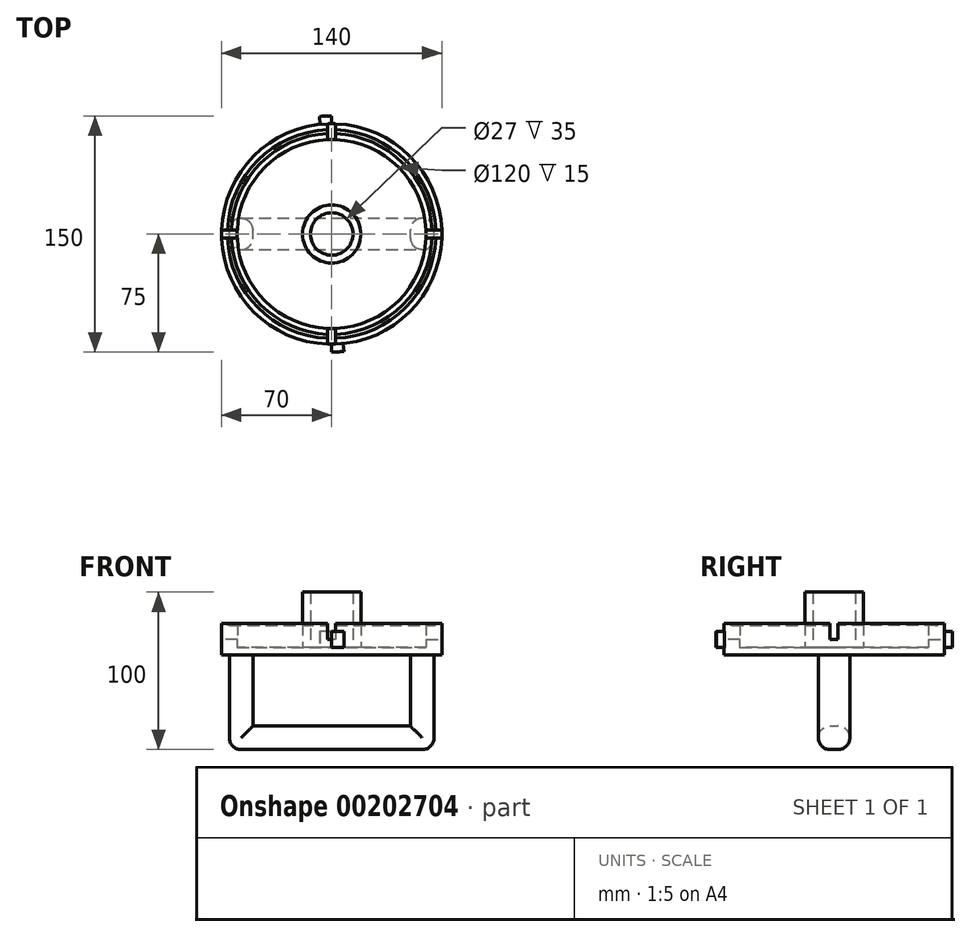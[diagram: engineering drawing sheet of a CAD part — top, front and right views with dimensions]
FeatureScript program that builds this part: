
annotation { "Feature Type Name" : "Feature", "Feature Type Description" : "" }
export const myFeature = defineFeature(function(context is Context, id is Id, definition is map)
    precondition{}
    {
        {
            var Q0;
            Q0=qCreatedBy(makeId("Top.planeOp"),FACE);
            var sketch = newSketch(context, id + "F0", { "sketchPlane" : qUnion([Q0])});
            skCircle(sketch, "E0", {"center": v(0, 0) * mm, "radius": 13.5 * mm});
            skCircle(sketch, "E1", {"center": v(0, 0) * mm, "radius": 18.5 * mm});
            skCircle(sketch, "E2", {"center": v(0, 0) * mm, "radius": 60 * mm});
            skCircle(sketch, "E3", {"center": v(0, 0) * mm, "radius": 70 * mm});
            skCircle(sketch, "E4", {"center": v(0, 0) * mm, "radius": 75 * mm});
            skLineSegment(sketch, "E5", {"start": v(0, 0) * mm, "end": v(0, 75) * mm});
            skLineSegment(sketch, "E6", {"start": v(0, 0) * mm, "end": v(0, -75) * mm});
            skLineSegment(sketch, "E7", {"start": v(0, 0) * mm, "end": v(-7.84, 74.59) * mm});
            skLineSegment(sketch, "E8", {"start": v(0, 0) * mm, "end": v(7.84, -74.59) * mm});
            skLineSegment(sketch, "E9.bottom", {"start": v(2.5, 2.5) * mm, "end": v(-2.5, 2.5) * mm});
            skLineSegment(sketch, "E9.top", {"start": v(2.5, -2.5) * mm, "end": v(-2.5, -2.5) * mm});
            skLineSegment(sketch, "E9.left", {"start": v(2.5, 2.5) * mm, "end": v(2.5, -2.5) * mm});
            skLineSegment(sketch, "E9.right", {"start": v(-2.5, 2.5) * mm, "end": v(-2.5, -2.5) * mm});
            skLineSegment(sketch, "E10", {"start": v(-2.5, -2.5) * mm, "end": v(-69.96, -2.5) * mm});
            skLineSegment(sketch, "E11", {"start": v(-2.5, 2.5) * mm, "end": v(-69.96, 2.5) * mm});
            skLineSegment(sketch, "E12", {"start": v(2.5, -2.5) * mm, "end": v(69.96, -2.5) * mm});
            skLineSegment(sketch, "E13", {"start": v(2.5, 2.5) * mm, "end": v(69.96, 2.5) * mm});
            skLineSegment(sketch, "E14", {"start": v(-2.5, -2.5) * mm, "end": v(-2.5, -69.96) * mm});
            skPoint(sketch, "E15.endSnap0", {"position": v(3.92, -37.3) * mm});
            skLineSegment(sketch, "E16", {"start": v(-2.5, 2.5) * mm, "end": v(-2.5, 69.96) * mm});
            skLineSegment(sketch, "E17", {"start": v(2.5, 2.5) * mm, "end": v(2.5, 69.96) * mm});
            skLineSegment(sketch, "E18", {"start": v(2.5, -2.5) * mm, "end": v(2.5, -69.96) * mm});
            skSolve(sketch);
        }
        {
            var Q0;
            {var subQ0=sQuery(id+"F0.wireOp",EDGE,"E5");var subQ1=sQuery(id+"F0.wireOp",EDGE,"E0");var subQ2=makeQuery(id+"F0.imprint","INTERSECT",VERTEX,{"derivedFrom":[subQ1,subQ0]});Q0=makeQuery(id+"F0.imprint","IMPRINT",FACE,{"disambiguationData":[TD([[makeQuery(id+"F0.imprint","IMPRINT",EDGE,{"disambiguationData":[TD([[subQ2,-1.0]])],"derivedFrom":subQ1}),1.0]])]});}
            var Q1;
            {var subQ0=sQuery(id+"F0.wireOp",EDGE,"E7");var subQ1=sQuery(id+"F0.wireOp",EDGE,"E0");var subQ2=makeQuery(id+"F0.imprint","INTERSECT",VERTEX,{"derivedFrom":[subQ1,subQ0]});Q1=makeQuery(id+"F0.imprint","IMPRINT",FACE,{"disambiguationData":[TD([[makeQuery(id+"F0.imprint","IMPRINT",EDGE,{"disambiguationData":[TD([[subQ2,-1.0]])],"derivedFrom":subQ1}),1.0]])]});}
            var Q2;
            {var subQ0=sQuery(id+"F0.wireOp",EDGE,"E17");var subQ1=sQuery(id+"F0.wireOp",EDGE,"E0");var subQ2=makeQuery(id+"F0.imprint","INTERSECT",VERTEX,{"derivedFrom":[subQ1,subQ0]});Q2=makeQuery(id+"F0.imprint","IMPRINT",FACE,{"disambiguationData":[TD([[makeQuery(id+"F0.imprint","IMPRINT",EDGE,{"disambiguationData":[TD([[subQ2,-1.0]])],"derivedFrom":subQ1}),1.0]])]});}
            var Q3;
            {var subQ0=sQuery(id+"F0.wireOp",EDGE,"E16");var subQ1=sQuery(id+"F0.wireOp",EDGE,"E0");var subQ2=makeQuery(id+"F0.imprint","INTERSECT",VERTEX,{"derivedFrom":[subQ1,subQ0]});Q3=makeQuery(id+"F0.imprint","IMPRINT",FACE,{"disambiguationData":[TD([[makeQuery(id+"F0.imprint","IMPRINT",EDGE,{"disambiguationData":[TD([[subQ2,-1.0]])],"derivedFrom":subQ1}),1.0]])]});}
            var Q4;
            {var subQ5=sQuery(id+"F0.wireOp",EDGE,"E9.right");Q4=makeQuery(id+"F0.imprint","IMPRINT",FACE,{"disambiguationData":[TD([[makeQuery(id+"F0.imprint","IMPRINT",EDGE,{"derivedFrom":subQ5}),-1.0]])]});}
            var Q5;
            {var subQ1=sQuery(id+"F0.wireOp",EDGE,"E5");var subQ3=sQuery(id+"F0.wireOp",EDGE,"E9.bottom");var subQ4=makeQuery(id+"F0.imprint","INTERSECT",VERTEX,{"derivedFrom":[subQ1,subQ3]});Q5=makeQuery(id+"F0.imprint","IMPRINT",FACE,{"disambiguationData":[TD([[makeQuery(id+"F0.imprint","IMPRINT",EDGE,{"disambiguationData":[TD([[subQ4,-1.0]])],"derivedFrom":subQ3}),1.0]])]});}
            var Q6;
            {var subQ1=sQuery(id+"F0.wireOp",EDGE,"E6");var subQ3=sQuery(id+"F0.wireOp",EDGE,"E9.top");var subQ4=makeQuery(id+"F0.imprint","INTERSECT",VERTEX,{"derivedFrom":[subQ1,subQ3]});Q6=makeQuery(id+"F0.imprint","IMPRINT",FACE,{"disambiguationData":[TD([[makeQuery(id+"F0.imprint","IMPRINT",EDGE,{"disambiguationData":[TD([[subQ4,1.0]])],"derivedFrom":subQ3}),-1.0]])]});}
            var Q7;
            {var subQ0=sQuery(id+"F0.wireOp",EDGE,"E9.right");Q7=makeQuery(id+"F0.imprint","IMPRINT",FACE,{"disambiguationData":[TD([[makeQuery(id+"F0.imprint","IMPRINT",EDGE,{"derivedFrom":subQ0}),1.0]])]});}
            var Q8;
            {var subQ0=sQuery(id+"F0.wireOp",EDGE,"E9.left");Q8=makeQuery(id+"F0.imprint","IMPRINT",FACE,{"disambiguationData":[TD([[makeQuery(id+"F0.imprint","IMPRINT",EDGE,{"derivedFrom":subQ0}),-1.0]])]});}
            var Q9;
            {var subQ5=sQuery(id+"F0.wireOp",EDGE,"E9.left");Q9=makeQuery(id+"F0.imprint","IMPRINT",FACE,{"disambiguationData":[TD([[makeQuery(id+"F0.imprint","IMPRINT",EDGE,{"derivedFrom":subQ5}),1.0]])]});}
            var Q10;
            {var subQ0=sQuery(id+"F0.wireOp",EDGE,"E17");var subQ1=sQuery(id+"F0.wireOp",EDGE,"E0");var subQ2=makeQuery(id+"F0.imprint","INTERSECT",VERTEX,{"derivedFrom":[subQ1,subQ0]});Q10=makeQuery(id+"F0.imprint","IMPRINT",FACE,{"disambiguationData":[TD([[makeQuery(id+"F0.imprint","IMPRINT",EDGE,{"disambiguationData":[TD([[subQ2,1.0]])],"derivedFrom":subQ1}),1.0]])]});}
            var Q11;
            {var subQ0=sQuery(id+"F0.wireOp",EDGE,"E10");var subQ1=sQuery(id+"F0.wireOp",EDGE,"E0");var subQ2=makeQuery(id+"F0.imprint","INTERSECT",VERTEX,{"derivedFrom":[subQ1,subQ0]});Q11=makeQuery(id+"F0.imprint","IMPRINT",FACE,{"disambiguationData":[TD([[makeQuery(id+"F0.imprint","IMPRINT",EDGE,{"disambiguationData":[TD([[subQ2,-1.0]])],"derivedFrom":subQ1}),1.0]])]});}
            var Q12;
            {var subQ0=sQuery(id+"F0.wireOp",EDGE,"E14");var subQ1=sQuery(id+"F0.wireOp",EDGE,"E0");var subQ2=makeQuery(id+"F0.imprint","INTERSECT",VERTEX,{"derivedFrom":[subQ1,subQ0]});Q12=makeQuery(id+"F0.imprint","IMPRINT",FACE,{"disambiguationData":[TD([[makeQuery(id+"F0.imprint","IMPRINT",EDGE,{"disambiguationData":[TD([[subQ2,-1.0]])],"derivedFrom":subQ1}),1.0]])]});}
            var Q13;
            {var subQ0=sQuery(id+"F0.wireOp",EDGE,"E6");var subQ1=sQuery(id+"F0.wireOp",EDGE,"E0");var subQ2=makeQuery(id+"F0.imprint","INTERSECT",VERTEX,{"derivedFrom":[subQ1,subQ0]});Q13=makeQuery(id+"F0.imprint","IMPRINT",FACE,{"disambiguationData":[TD([[makeQuery(id+"F0.imprint","IMPRINT",EDGE,{"disambiguationData":[TD([[subQ2,-1.0]])],"derivedFrom":subQ1}),1.0]])]});}
            var Q14;
            {var subQ0=sQuery(id+"F0.wireOp",EDGE,"E8");var subQ1=sQuery(id+"F0.wireOp",EDGE,"E0");var subQ2=makeQuery(id+"F0.imprint","INTERSECT",VERTEX,{"derivedFrom":[subQ1,subQ0]});Q14=makeQuery(id+"F0.imprint","IMPRINT",FACE,{"disambiguationData":[TD([[makeQuery(id+"F0.imprint","IMPRINT",EDGE,{"disambiguationData":[TD([[subQ2,-1.0]])],"derivedFrom":subQ1}),1.0]])]});}
            var Q15;
            {var subQ0=sQuery(id+"F0.wireOp",EDGE,"E15");var subQ1=sQuery(id+"F0.wireOp",EDGE,"E0");var subQ2=makeQuery(id+"F0.imprint","INTERSECT",VERTEX,{"derivedFrom":[subQ1,subQ0]});Q15=makeQuery(id+"F0.imprint","IMPRINT",FACE,{"disambiguationData":[TD([[makeQuery(id+"F0.imprint","IMPRINT",EDGE,{"disambiguationData":[TD([[subQ2,-1.0]])],"derivedFrom":subQ1}),1.0]])]});}
            extrude(context, id + "F1", {"entities" : qUnion([Q0, Q1, Q2, Q3, Q4, Q5, Q6, Q7, Q8, Q9, Q10, Q11, Q12, Q13, Q14, Q15]), "depth" : 5 * mm});
        }
        {
            var Q0;
            {var subQ0=sQuery(id+"F0.wireOp",EDGE,"E10");var subQ1=sQuery(id+"F0.wireOp",EDGE,"E0");var subQ2=makeQuery(id+"F0.imprint","INTERSECT",VERTEX,{"derivedFrom":[subQ1,subQ0]});Q0=makeQuery(id+"F0.imprint","IMPRINT",FACE,{"disambiguationData":[TD([[makeQuery(id+"F0.imprint","IMPRINT",EDGE,{"disambiguationData":[TD([[subQ2,-1.0]])],"derivedFrom":subQ1}),-1.0]])]});}
            var Q1;
            {var subQ0=sQuery(id+"F0.wireOp",EDGE,"E14");var subQ1=sQuery(id+"F0.wireOp",EDGE,"E0");var subQ2=makeQuery(id+"F0.imprint","INTERSECT",VERTEX,{"derivedFrom":[subQ1,subQ0]});Q1=makeQuery(id+"F0.imprint","IMPRINT",FACE,{"disambiguationData":[TD([[makeQuery(id+"F0.imprint","IMPRINT",EDGE,{"disambiguationData":[TD([[subQ2,-1.0]])],"derivedFrom":subQ1}),-1.0]])]});}
            var Q2;
            {var subQ0=sQuery(id+"F0.wireOp",EDGE,"E6");var subQ1=sQuery(id+"F0.wireOp",EDGE,"E0");var subQ2=makeQuery(id+"F0.imprint","INTERSECT",VERTEX,{"derivedFrom":[subQ1,subQ0]});Q2=makeQuery(id+"F0.imprint","IMPRINT",FACE,{"disambiguationData":[TD([[makeQuery(id+"F0.imprint","IMPRINT",EDGE,{"disambiguationData":[TD([[subQ2,-1.0]])],"derivedFrom":subQ1}),-1.0]])]});}
            var Q3;
            {var subQ0=sQuery(id+"F0.wireOp",EDGE,"E8");var subQ1=sQuery(id+"F0.wireOp",EDGE,"E0");var subQ2=makeQuery(id+"F0.imprint","INTERSECT",VERTEX,{"derivedFrom":[subQ1,subQ0]});Q3=makeQuery(id+"F0.imprint","IMPRINT",FACE,{"disambiguationData":[TD([[makeQuery(id+"F0.imprint","IMPRINT",EDGE,{"disambiguationData":[TD([[subQ2,-1.0]])],"derivedFrom":subQ1}),-1.0]])]});}
            var Q4;
            {var subQ0=sQuery(id+"F0.wireOp",EDGE,"E15");var subQ1=sQuery(id+"F0.wireOp",EDGE,"E0");var subQ2=makeQuery(id+"F0.imprint","INTERSECT",VERTEX,{"derivedFrom":[subQ1,subQ0]});Q4=makeQuery(id+"F0.imprint","IMPRINT",FACE,{"disambiguationData":[TD([[makeQuery(id+"F0.imprint","IMPRINT",EDGE,{"disambiguationData":[TD([[subQ2,-1.0]])],"derivedFrom":subQ1}),-1.0]])]});}
            var Q5;
            {var subQ0=sQuery(id+"F0.wireOp",EDGE,"E13");var subQ1=sQuery(id+"F0.wireOp",EDGE,"E0");var subQ2=makeQuery(id+"F0.imprint","INTERSECT",VERTEX,{"derivedFrom":[subQ1,subQ0]});Q5=makeQuery(id+"F0.imprint","IMPRINT",FACE,{"disambiguationData":[TD([[makeQuery(id+"F0.imprint","IMPRINT",EDGE,{"disambiguationData":[TD([[subQ2,1.0]])],"derivedFrom":subQ1}),-1.0]])]});}
            var Q6;
            {var subQ0=sQuery(id+"F0.wireOp",EDGE,"E17");var subQ1=sQuery(id+"F0.wireOp",EDGE,"E0");var subQ2=makeQuery(id+"F0.imprint","INTERSECT",VERTEX,{"derivedFrom":[subQ1,subQ0]});Q6=makeQuery(id+"F0.imprint","IMPRINT",FACE,{"disambiguationData":[TD([[makeQuery(id+"F0.imprint","IMPRINT",EDGE,{"disambiguationData":[TD([[subQ2,1.0]])],"derivedFrom":subQ1}),-1.0]])]});}
            var Q7;
            {var subQ0=sQuery(id+"F0.wireOp",EDGE,"E17");var subQ1=sQuery(id+"F0.wireOp",EDGE,"E0");var subQ2=makeQuery(id+"F0.imprint","INTERSECT",VERTEX,{"derivedFrom":[subQ1,subQ0]});Q7=makeQuery(id+"F0.imprint","IMPRINT",FACE,{"disambiguationData":[TD([[makeQuery(id+"F0.imprint","IMPRINT",EDGE,{"disambiguationData":[TD([[subQ2,-1.0]])],"derivedFrom":subQ1}),-1.0]])]});}
            var Q8;
            {var subQ0=sQuery(id+"F0.wireOp",EDGE,"E5");var subQ1=sQuery(id+"F0.wireOp",EDGE,"E0");var subQ2=makeQuery(id+"F0.imprint","INTERSECT",VERTEX,{"derivedFrom":[subQ1,subQ0]});Q8=makeQuery(id+"F0.imprint","IMPRINT",FACE,{"disambiguationData":[TD([[makeQuery(id+"F0.imprint","IMPRINT",EDGE,{"disambiguationData":[TD([[subQ2,-1.0]])],"derivedFrom":subQ1}),-1.0]])]});}
            var Q9;
            {var subQ0=sQuery(id+"F0.wireOp",EDGE,"E7");var subQ1=sQuery(id+"F0.wireOp",EDGE,"E0");var subQ2=makeQuery(id+"F0.imprint","INTERSECT",VERTEX,{"derivedFrom":[subQ1,subQ0]});Q9=makeQuery(id+"F0.imprint","IMPRINT",FACE,{"disambiguationData":[TD([[makeQuery(id+"F0.imprint","IMPRINT",EDGE,{"disambiguationData":[TD([[subQ2,-1.0]])],"derivedFrom":subQ1}),-1.0]])]});}
            var Q10;
            {var subQ0=sQuery(id+"F0.wireOp",EDGE,"E16");var subQ1=sQuery(id+"F0.wireOp",EDGE,"E0");var subQ2=makeQuery(id+"F0.imprint","INTERSECT",VERTEX,{"derivedFrom":[subQ1,subQ0]});Q10=makeQuery(id+"F0.imprint","IMPRINT",FACE,{"disambiguationData":[TD([[makeQuery(id+"F0.imprint","IMPRINT",EDGE,{"disambiguationData":[TD([[subQ2,-1.0]])],"derivedFrom":subQ1}),-1.0]])]});}
            var Q11;
            {var subQ0=sQuery(id+"F0.wireOp",EDGE,"E11");var subQ1=sQuery(id+"F0.wireOp",EDGE,"E0");var subQ2=makeQuery(id+"F0.imprint","INTERSECT",VERTEX,{"derivedFrom":[subQ1,subQ0]});Q11=makeQuery(id+"F0.imprint","IMPRINT",FACE,{"disambiguationData":[TD([[makeQuery(id+"F0.imprint","IMPRINT",EDGE,{"disambiguationData":[TD([[subQ2,-1.0]])],"derivedFrom":subQ1}),-1.0]])]});}
            extrude(context, id + "F2", {"entities" : qUnion([Q0, Q1, Q2, Q3, Q4, Q5, Q6, Q7, Q8, Q9, Q10, Q11]), "operationType" : NewBodyOperationType.ADD, "depth" : 40 * mm});
        }
        {
            var Q0;
            {var subQ0=sQuery(id+"F0.wireOp",EDGE,"E11");var subQ1=sQuery(id+"F0.wireOp",EDGE,"E1");var subQ2=makeQuery(id+"F0.imprint","INTERSECT",VERTEX,{"derivedFrom":[subQ1,subQ0]});Q0=makeQuery(id+"F0.imprint","IMPRINT",FACE,{"disambiguationData":[TD([[makeQuery(id+"F0.imprint","IMPRINT",EDGE,{"disambiguationData":[TD([[subQ2,-1.0]])],"derivedFrom":subQ1}),-1.0]])]});}
            var Q1;
            {var subQ1=sQuery(id+"F0.wireOp",EDGE,"E1");var subQ7=sQuery(id+"F0.wireOp",EDGE,"E16");var subQ9=makeQuery(id+"F0.imprint","INTERSECT",VERTEX,{"derivedFrom":[subQ1,subQ7]});Q1=makeQuery(id+"F0.imprint","IMPRINT",FACE,{"disambiguationData":[TD([[makeQuery(id+"F0.imprint","IMPRINT",EDGE,{"disambiguationData":[TD([[subQ9,-1.0]])],"derivedFrom":subQ1}),-1.0]])]});}
            var Q2;
            {var subQ0=sQuery(id+"F0.wireOp",EDGE,"E16");var subQ1=sQuery(id+"F0.wireOp",EDGE,"E2");var subQ2=makeQuery(id+"F0.imprint","INTERSECT",VERTEX,{"derivedFrom":[subQ1,subQ0]});Q2=makeQuery(id+"F0.imprint","IMPRINT",FACE,{"disambiguationData":[TD([[makeQuery(id+"F0.imprint","IMPRINT",EDGE,{"disambiguationData":[TD([[subQ2,-1.0]])],"derivedFrom":subQ1}),1.0]])]});}
            var Q3;
            {var subQ1=sQuery(id+"F0.wireOp",EDGE,"E1");var subQ5=sQuery(id+"F0.wireOp",EDGE,"E5");var subQ6=makeQuery(id+"F0.imprint","INTERSECT",VERTEX,{"derivedFrom":[subQ1,subQ5]});Q3=makeQuery(id+"F0.imprint","IMPRINT",FACE,{"disambiguationData":[TD([[makeQuery(id+"F0.imprint","IMPRINT",EDGE,{"disambiguationData":[TD([[subQ6,-1.0]])],"derivedFrom":subQ1}),-1.0]])]});}
            var Q4;
            {var subQ0=sQuery(id+"F0.wireOp",EDGE,"E17");var subQ1=sQuery(id+"F0.wireOp",EDGE,"E1");var subQ2=makeQuery(id+"F0.imprint","INTERSECT",VERTEX,{"derivedFrom":[subQ1,subQ0]});Q4=makeQuery(id+"F0.imprint","IMPRINT",FACE,{"disambiguationData":[TD([[makeQuery(id+"F0.imprint","IMPRINT",EDGE,{"disambiguationData":[TD([[subQ2,-1.0]])],"derivedFrom":subQ1}),-1.0]])]});}
            var Q5;
            {var subQ0=sQuery(id+"F0.wireOp",EDGE,"E17");var subQ1=sQuery(id+"F0.wireOp",EDGE,"E1");var subQ2=makeQuery(id+"F0.imprint","INTERSECT",VERTEX,{"derivedFrom":[subQ1,subQ0]});Q5=makeQuery(id+"F0.imprint","IMPRINT",FACE,{"disambiguationData":[TD([[makeQuery(id+"F0.imprint","IMPRINT",EDGE,{"disambiguationData":[TD([[subQ2,1.0]])],"derivedFrom":subQ1}),-1.0]])]});}
            var Q6;
            {var subQ0=sQuery(id+"F0.wireOp",EDGE,"E13");var subQ1=sQuery(id+"F0.wireOp",EDGE,"E1");var subQ2=makeQuery(id+"F0.imprint","INTERSECT",VERTEX,{"derivedFrom":[subQ1,subQ0]});Q6=makeQuery(id+"F0.imprint","IMPRINT",FACE,{"disambiguationData":[TD([[makeQuery(id+"F0.imprint","IMPRINT",EDGE,{"disambiguationData":[TD([[subQ2,1.0]])],"derivedFrom":subQ1}),-1.0]])]});}
            var Q7;
            {var subQ3=sQuery(id+"F0.wireOp",EDGE,"E15");var subQ6=sQuery(id+"F0.wireOp",EDGE,"E1");var subQ9=makeQuery(id+"F0.imprint","INTERSECT",VERTEX,{"derivedFrom":[subQ6,subQ3]});Q7=makeQuery(id+"F0.imprint","IMPRINT",FACE,{"disambiguationData":[TD([[makeQuery(id+"F0.imprint","IMPRINT",EDGE,{"disambiguationData":[TD([[subQ9,-1.0]])],"derivedFrom":subQ6}),-1.0]])]});}
            var Q8;
            {var subQ0=sQuery(id+"F0.wireOp",EDGE,"E10");var subQ1=sQuery(id+"F0.wireOp",EDGE,"E1");var subQ2=makeQuery(id+"F0.imprint","INTERSECT",VERTEX,{"derivedFrom":[subQ1,subQ0]});Q8=makeQuery(id+"F0.imprint","IMPRINT",FACE,{"disambiguationData":[TD([[makeQuery(id+"F0.imprint","IMPRINT",EDGE,{"disambiguationData":[TD([[subQ2,-1.0]])],"derivedFrom":subQ1}),-1.0]])]});}
            var Q9;
            {var subQ0=sQuery(id+"F0.wireOp",EDGE,"E14");var subQ1=sQuery(id+"F0.wireOp",EDGE,"E1");var subQ2=makeQuery(id+"F0.imprint","INTERSECT",VERTEX,{"derivedFrom":[subQ1,subQ0]});Q9=makeQuery(id+"F0.imprint","IMPRINT",FACE,{"disambiguationData":[TD([[makeQuery(id+"F0.imprint","IMPRINT",EDGE,{"disambiguationData":[TD([[subQ2,-1.0]])],"derivedFrom":subQ1}),-1.0]])]});}
            var Q10;
            {var subQ1=sQuery(id+"F0.wireOp",EDGE,"E1");var subQ5=sQuery(id+"F0.wireOp",EDGE,"E6");var subQ6=makeQuery(id+"F0.imprint","INTERSECT",VERTEX,{"derivedFrom":[subQ1,subQ5]});Q10=makeQuery(id+"F0.imprint","IMPRINT",FACE,{"disambiguationData":[TD([[makeQuery(id+"F0.imprint","IMPRINT",EDGE,{"disambiguationData":[TD([[subQ6,-1.0]])],"derivedFrom":subQ1}),-1.0]])]});}
            var Q11;
            {var subQ0=sQuery(id+"F0.wireOp",EDGE,"E15");var subQ1=sQuery(id+"F0.wireOp",EDGE,"E2");var subQ2=makeQuery(id+"F0.imprint","INTERSECT",VERTEX,{"derivedFrom":[subQ1,subQ0]});Q11=makeQuery(id+"F0.imprint","IMPRINT",FACE,{"disambiguationData":[TD([[makeQuery(id+"F0.imprint","IMPRINT",EDGE,{"disambiguationData":[TD([[subQ2,-1.0]])],"derivedFrom":subQ1}),1.0]])]});}
            var Q12;
            {var subQ0=sQuery(id+"F0.wireOp",EDGE,"E8");var subQ1=sQuery(id+"F0.wireOp",EDGE,"E1");var subQ2=makeQuery(id+"F0.imprint","INTERSECT",VERTEX,{"derivedFrom":[subQ1,subQ0]});Q12=makeQuery(id+"F0.imprint","IMPRINT",FACE,{"disambiguationData":[TD([[makeQuery(id+"F0.imprint","IMPRINT",EDGE,{"disambiguationData":[TD([[subQ2,-1.0]])],"derivedFrom":subQ1}),-1.0]])]});}
            var Q13;
            {var subQ0=sQuery(id+"F0.wireOp",EDGE,"E7");var subQ1=sQuery(id+"F0.wireOp",EDGE,"E1");var subQ2=makeQuery(id+"F0.imprint","INTERSECT",VERTEX,{"derivedFrom":[subQ1,subQ0]});Q13=makeQuery(id+"F0.imprint","IMPRINT",FACE,{"disambiguationData":[TD([[makeQuery(id+"F0.imprint","IMPRINT",EDGE,{"disambiguationData":[TD([[subQ2,-1.0]])],"derivedFrom":subQ1}),-1.0]])]});}
            var Q14;
            {var subQ3=sQuery(id+"F0.wireOp",EDGE,"E18");var subQ6=sQuery(id+"F0.wireOp",EDGE,"E1");var subQ9=makeQuery(id+"F0.imprint","INTERSECT",VERTEX,{"derivedFrom":[subQ6,subQ3]});Q14=makeQuery(id+"F0.imprint","IMPRINT",FACE,{"disambiguationData":[TD([[makeQuery(id+"F0.imprint","IMPRINT",EDGE,{"disambiguationData":[TD([[subQ9,-1.0]])],"derivedFrom":subQ6}),-1.0]])]});}
            extrude(context, id + "F3", {"entities" : qUnion([Q0, Q1, Q2, Q3, Q4, Q5, Q6, Q7, Q8, Q9, Q10, Q11, Q12, Q13, Q14]), "operationType" : NewBodyOperationType.ADD, "depth" : 5 * mm});
        }
        {
            var Q0;
            {var subQ0=sQuery(id+"F0.wireOp",EDGE,"E17");var subQ1=sQuery(id+"F0.wireOp",EDGE,"E2");var subQ2=makeQuery(id+"F0.imprint","INTERSECT",VERTEX,{"derivedFrom":[subQ1,subQ0]});Q0=makeQuery(id+"F0.imprint","IMPRINT",FACE,{"disambiguationData":[TD([[makeQuery(id+"F0.imprint","IMPRINT",EDGE,{"disambiguationData":[TD([[subQ2,1.0]])],"derivedFrom":subQ1}),-1.0]])]});}
            var Q1;
            {var subQ0=sQuery(id+"F0.wireOp",EDGE,"E16");var subQ1=sQuery(id+"F0.wireOp",EDGE,"E2");var subQ2=makeQuery(id+"F0.imprint","INTERSECT",VERTEX,{"derivedFrom":[subQ1,subQ0]});Q1=makeQuery(id+"F0.imprint","IMPRINT",FACE,{"disambiguationData":[TD([[makeQuery(id+"F0.imprint","IMPRINT",EDGE,{"disambiguationData":[TD([[subQ2,-1.0]])],"derivedFrom":subQ1}),-1.0]])]});}
            var Q2;
            {var subQ0=sQuery(id+"F0.wireOp",EDGE,"E7");var subQ1=sQuery(id+"F0.wireOp",EDGE,"E2");var subQ2=makeQuery(id+"F0.imprint","INTERSECT",VERTEX,{"derivedFrom":[subQ1,subQ0]});Q2=makeQuery(id+"F0.imprint","IMPRINT",FACE,{"disambiguationData":[TD([[makeQuery(id+"F0.imprint","IMPRINT",EDGE,{"disambiguationData":[TD([[subQ2,-1.0]])],"derivedFrom":subQ1}),-1.0]])]});}
            var Q3;
            {var subQ0=sQuery(id+"F0.wireOp",EDGE,"E10");var subQ1=sQuery(id+"F0.wireOp",EDGE,"E2");var subQ2=makeQuery(id+"F0.imprint","INTERSECT",VERTEX,{"derivedFrom":[subQ1,subQ0]});Q3=makeQuery(id+"F0.imprint","IMPRINT",FACE,{"disambiguationData":[TD([[makeQuery(id+"F0.imprint","IMPRINT",EDGE,{"disambiguationData":[TD([[subQ2,-1.0]])],"derivedFrom":subQ1}),-1.0]])]});}
            var Q4;
            {var subQ0=sQuery(id+"F0.wireOp",EDGE,"E18");var subQ1=sQuery(id+"F0.wireOp",EDGE,"E2");var subQ2=makeQuery(id+"F0.imprint","INTERSECT",VERTEX,{"derivedFrom":[subQ1,subQ0]});Q4=makeQuery(id+"F0.imprint","IMPRINT",FACE,{"disambiguationData":[TD([[makeQuery(id+"F0.imprint","IMPRINT",EDGE,{"disambiguationData":[TD([[subQ2,-1.0]])],"derivedFrom":subQ1}),-1.0]])]});}
            var Q5;
            {var subQ0=sQuery(id+"F0.wireOp",EDGE,"E8");var subQ1=sQuery(id+"F0.wireOp",EDGE,"E2");var subQ2=makeQuery(id+"F0.imprint","INTERSECT",VERTEX,{"derivedFrom":[subQ1,subQ0]});Q5=makeQuery(id+"F0.imprint","IMPRINT",FACE,{"disambiguationData":[TD([[makeQuery(id+"F0.imprint","IMPRINT",EDGE,{"disambiguationData":[TD([[subQ2,-1.0]])],"derivedFrom":subQ1}),-1.0]])]});}
            var Q6;
            {var subQ0=sQuery(id+"F0.wireOp",EDGE,"E10");var subQ1=sQuery(id+"F0.wireOp",EDGE,"E2");var subQ2=makeQuery(id+"F0.imprint","INTERSECT",VERTEX,{"derivedFrom":[subQ1,subQ0]});Q6=makeQuery(id+"F0.imprint","IMPRINT",FACE,{"disambiguationData":[TD([[makeQuery(id+"F0.imprint","IMPRINT",EDGE,{"disambiguationData":[TD([[subQ2,-1.0]])],"derivedFrom":subQ1}),-1.0]])]});}
            var Q7;
            {var subQ0=sQuery(id+"F0.wireOp",EDGE,"E7");var subQ1=sQuery(id+"F0.wireOp",EDGE,"E2");var subQ2=makeQuery(id+"F0.imprint","INTERSECT",VERTEX,{"derivedFrom":[subQ1,subQ0]});Q7=makeQuery(id+"F0.imprint","IMPRINT",FACE,{"disambiguationData":[TD([[makeQuery(id+"F0.imprint","IMPRINT",EDGE,{"disambiguationData":[TD([[subQ2,-1.0]])],"derivedFrom":subQ1}),-1.0]])]});}
            var Q8;
            {var subQ0=sQuery(id+"F0.wireOp",EDGE,"E8");var subQ1=sQuery(id+"F0.wireOp",EDGE,"E2");var subQ2=makeQuery(id+"F0.imprint","INTERSECT",VERTEX,{"derivedFrom":[subQ1,subQ0]});Q8=makeQuery(id+"F0.imprint","IMPRINT",FACE,{"disambiguationData":[TD([[makeQuery(id+"F0.imprint","IMPRINT",EDGE,{"disambiguationData":[TD([[subQ2,-1.0]])],"derivedFrom":subQ1}),-1.0]])]});}
            var Q9;
            {var subQ0=sQuery(id+"F0.wireOp",EDGE,"E16");var subQ1=sQuery(id+"F0.wireOp",EDGE,"E2");var subQ2=makeQuery(id+"F0.imprint","INTERSECT",VERTEX,{"derivedFrom":[subQ1,subQ0]});Q9=makeQuery(id+"F0.imprint","IMPRINT",FACE,{"disambiguationData":[TD([[makeQuery(id+"F0.imprint","IMPRINT",EDGE,{"disambiguationData":[TD([[subQ2,-1.0]])],"derivedFrom":subQ1}),-1.0]])]});}
            extrude(context, id + "F4", {"entities" : qUnion([Q0, Q1, Q2, Q3, Q4, Q5, Q6, Q7, Q8, Q9]), "operationType" : NewBodyOperationType.ADD, "depth" : 20 * mm});
        }
        {
            var Q0;
            {var subQ0=sQuery(id+"F0.wireOp",EDGE,"E11");var subQ1=sQuery(id+"F0.wireOp",EDGE,"E2");var subQ2=makeQuery(id+"F0.imprint","INTERSECT",VERTEX,{"derivedFrom":[subQ1,subQ0]});Q0=makeQuery(id+"F0.imprint","IMPRINT",FACE,{"disambiguationData":[TD([[makeQuery(id+"F0.imprint","IMPRINT",EDGE,{"disambiguationData":[TD([[subQ2,-1.0]])],"derivedFrom":subQ1}),-1.0]])]});}
            var Q1;
            {var subQ0=sQuery(id+"F0.wireOp",EDGE,"E6");var subQ1=sQuery(id+"F0.wireOp",EDGE,"E2");var subQ2=makeQuery(id+"F0.imprint","INTERSECT",VERTEX,{"derivedFrom":[subQ1,subQ0]});Q1=makeQuery(id+"F0.imprint","IMPRINT",FACE,{"disambiguationData":[TD([[makeQuery(id+"F0.imprint","IMPRINT",EDGE,{"disambiguationData":[TD([[subQ2,-1.0]])],"derivedFrom":subQ1}),-1.0]])]});}
            var Q2;
            {var subQ0=sQuery(id+"F0.wireOp",EDGE,"E14");var subQ1=sQuery(id+"F0.wireOp",EDGE,"E2");var subQ2=makeQuery(id+"F0.imprint","INTERSECT",VERTEX,{"derivedFrom":[subQ1,subQ0]});Q2=makeQuery(id+"F0.imprint","IMPRINT",FACE,{"disambiguationData":[TD([[makeQuery(id+"F0.imprint","IMPRINT",EDGE,{"disambiguationData":[TD([[subQ2,-1.0]])],"derivedFrom":subQ1}),-1.0]])]});}
            var Q3;
            {var subQ0=sQuery(id+"F0.wireOp",EDGE,"E13");var subQ1=sQuery(id+"F0.wireOp",EDGE,"E2");var subQ2=makeQuery(id+"F0.imprint","INTERSECT",VERTEX,{"derivedFrom":[subQ1,subQ0]});Q3=makeQuery(id+"F0.imprint","IMPRINT",FACE,{"disambiguationData":[TD([[makeQuery(id+"F0.imprint","IMPRINT",EDGE,{"disambiguationData":[TD([[subQ2,1.0]])],"derivedFrom":subQ1}),-1.0]])]});}
            var Q4;
            {var subQ0=sQuery(id+"F0.wireOp",EDGE,"E17");var subQ1=sQuery(id+"F0.wireOp",EDGE,"E2");var subQ2=makeQuery(id+"F0.imprint","INTERSECT",VERTEX,{"derivedFrom":[subQ1,subQ0]});Q4=makeQuery(id+"F0.imprint","IMPRINT",FACE,{"disambiguationData":[TD([[makeQuery(id+"F0.imprint","IMPRINT",EDGE,{"disambiguationData":[TD([[subQ2,-1.0]])],"derivedFrom":subQ1}),-1.0]])]});}
            var Q5;
            {var subQ0=sQuery(id+"F0.wireOp",EDGE,"E5");var subQ1=sQuery(id+"F0.wireOp",EDGE,"E2");var subQ2=makeQuery(id+"F0.imprint","INTERSECT",VERTEX,{"derivedFrom":[subQ1,subQ0]});Q5=makeQuery(id+"F0.imprint","IMPRINT",FACE,{"disambiguationData":[TD([[makeQuery(id+"F0.imprint","IMPRINT",EDGE,{"disambiguationData":[TD([[subQ2,-1.0]])],"derivedFrom":subQ1}),-1.0]])]});}
            extrude(context, id + "F5", {"entities" : qUnion([Q0, Q1, Q2, Q3, Q4, Q5]), "operationType" : NewBodyOperationType.ADD, "depth" : 10 * mm});
        }
        {
            var Q0;
            {var subQ3=sQuery(id+"F0.wireOp",EDGE,"E3");var subQ5=makeQuery(id+"F0.imprint","INTERSECT",VERTEX,{"derivedFrom":[subQ3,sQuery(id+"F0.wireOp",EDGE,"E18")]});Q0=makeQuery(id+"F0.imprint","IMPRINT",FACE,{"disambiguationData":[TD([[makeQuery(id+"F0.imprint","IMPRINT",EDGE,{"disambiguationData":[TD([[subQ5,1.0]])],"derivedFrom":subQ3}),-1.0]])]});}
            var Q1;
            {var subQ3=sQuery(id+"F0.wireOp",EDGE,"E3");var subQ7=makeQuery(id+"F0.imprint","INTERSECT",VERTEX,{"derivedFrom":[subQ3,sQuery(id+"F0.wireOp",EDGE,"E16")]});Q1=makeQuery(id+"F0.imprint","IMPRINT",FACE,{"disambiguationData":[TD([[makeQuery(id+"F0.imprint","IMPRINT",EDGE,{"disambiguationData":[TD([[subQ7,1.0]])],"derivedFrom":subQ3}),-1.0]])]});}
            extrude(context, id + "F6", {"entities" : qUnion([Q0, Q1]), "operationType" : NewBodyOperationType.ADD, "depth" : 15 * mm});
        }
        {
            var Q0;
            {var subQ3=sQuery(id+"F0.wireOp",EDGE,"E3");var subQ7=makeQuery(id+"F0.imprint","INTERSECT",VERTEX,{"derivedFrom":[subQ3,sQuery(id+"F0.wireOp",EDGE,"E16")]});Q0=makeQuery(id+"F0.imprint","IMPRINT",FACE,{"disambiguationData":[TD([[makeQuery(id+"F0.imprint","IMPRINT",EDGE,{"disambiguationData":[TD([[subQ7,1.0]])],"derivedFrom":subQ3}),-1.0]])]});}
            var Q1;
            {var subQ3=sQuery(id+"F0.wireOp",EDGE,"E3");var subQ5=makeQuery(id+"F0.imprint","INTERSECT",VERTEX,{"derivedFrom":[subQ3,sQuery(id+"F0.wireOp",EDGE,"E18")]});Q1=makeQuery(id+"F0.imprint","IMPRINT",FACE,{"disambiguationData":[TD([[makeQuery(id+"F0.imprint","IMPRINT",EDGE,{"disambiguationData":[TD([[subQ5,1.0]])],"derivedFrom":subQ3}),-1.0]])]});}
            extrude(context, id + "F7", {"entities" : qUnion([Q0, Q1]), "operationType" : NewBodyOperationType.REMOVE, "depth" : 5 * mm});
        }
        {
            var Q0;
            {var subQ0=sQuery(id+"F0.wireOp",EDGE,"E4");var subQ1=sQuery(id+"F0.wireOp",EDGE,"E3");var subQ2=sQuery(id+"F0.wireOp",EDGE,"E13");var subQ3=sQuery(id+"F0.wireOp",EDGE,"E12");var subQ4=sQuery(id+"F0.wireOp",EDGE,"E2");var subQ5=sQuery(id+"F0.wireOp",EDGE,"E18");var subQ6=sQuery(id+"F0.wireOp",EDGE,"E14");var subQ7=sQuery(id+"F0.wireOp",EDGE,"E11");var subQ8=sQuery(id+"F0.wireOp",EDGE,"E10");var subQ9=sQuery(id+"F0.wireOp",EDGE,"E17");var subQ10=sQuery(id+"F0.wireOp",EDGE,"E16");var subQ11=sQuery(id+"F0.wireOp",EDGE,"E1");var subQ12=sQuery(id+"F0.wireOp",EDGE,"E0");Q0=makeQuery(id+"F6.boolean.opBoolean","MERGE",FACE,{"derivedFrom":[makeQuery(id+"F5.boolean.opBoolean","MERGE",FACE,{"derivedFrom":[makeQuery(id+"F4.boolean.opBoolean","MERGE",FACE,{"derivedFrom":[makeQuery(id+"F3.boolean.opBoolean","MERGE",FACE,{"derivedFrom":[makeQuery(id+"F2.boolean.opBoolean","MERGE",FACE,{"derivedFrom":[makeQuery(id+"F1.opExtrude","CAP_FACE",FACE,{"disambiguationData":[OSD([subQ12])],"isStart":true}),makeQuery(id+"F2.opExtrude","CAP_FACE",FACE,{"disambiguationData":[OSD([subQ12,subQ11])],"isStart":true})]}),makeQuery(id+"F3.opExtrude","CAP_FACE",FACE,{"disambiguationData":[OSD([subQ11,subQ4])],"isStart":true})]}),makeQuery(id+"F4.opExtrude","CAP_FACE",FACE,{"disambiguationData":[OSD([subQ4,subQ1,subQ2,subQ9])],"isStart":true}),makeQuery(id+"F4.opExtrude","CAP_FACE",FACE,{"disambiguationData":[OSD([subQ4,subQ1,subQ7,subQ10])],"isStart":true}),makeQuery(id+"F4.opExtrude","CAP_FACE",FACE,{"disambiguationData":[OSD([subQ4,subQ1,subQ8,subQ6])],"isStart":true}),makeQuery(id+"F4.opExtrude","CAP_FACE",FACE,{"disambiguationData":[OSD([subQ4,subQ1,subQ3,subQ5])],"isStart":true})]}),makeQuery(id+"F5.opExtrude","CAP_FACE",FACE,{"disambiguationData":[OSD([subQ4,subQ1,subQ10,subQ9])],"isStart":true}),makeQuery(id+"F5.opExtrude","CAP_FACE",FACE,{"disambiguationData":[OSD([subQ4,subQ1,subQ8,subQ7])],"isStart":true}),makeQuery(id+"F5.opExtrude","CAP_FACE",FACE,{"disambiguationData":[OSD([subQ4,subQ1,subQ6,subQ5])],"isStart":true}),makeQuery(id+"F5.opExtrude","CAP_FACE",FACE,{"disambiguationData":[OSD([subQ4,subQ1,subQ3,subQ2])],"isStart":true})]}),makeQuery(id+"F6.opExtrude","CAP_FACE",FACE,{"disambiguationData":[OSD([subQ1,subQ0,sQuery(id+"F0.wireOp",EDGE,"E5"),sQuery(id+"F0.wireOp",EDGE,"E7")])],"isStart":true}),makeQuery(id+"F6.opExtrude","CAP_FACE",FACE,{"disambiguationData":[OSD([subQ1,subQ0,sQuery(id+"F0.wireOp",EDGE,"E6"),sQuery(id+"F0.wireOp",EDGE,"E8")])],"isStart":true})]});}
            var sketch = newSketch(context, id + "F8", { "sketchPlane" : qUnion([Q0])});
            skLineSegment(sketch, "E19.left", {"start": v(50, 10) * mm, "end": v(50, -10) * mm});
            skPoint(sketch, "E19.middle", {"position": v(0, 0) * mm});
            skLineSegment(sketch, "E20.bottom", {"start": v(50, 10) * mm, "end": v(65, 10) * mm});
            skLineSegment(sketch, "E20.top", {"start": v(50, -10) * mm, "end": v(65, -10) * mm});
            skLineSegment(sketch, "E20.right", {"start": v(65, 10) * mm, "end": v(65, -10) * mm});
            skLineSegment(sketch, "E21.bottom", {"start": v(-50, 10) * mm, "end": v(-65, 10) * mm});
            skLineSegment(sketch, "E21.top", {"start": v(-50, -10) * mm, "end": v(-65, -10) * mm});
            skLineSegment(sketch, "E21.left", {"start": v(-50, 10) * mm, "end": v(-50, -10) * mm});
            skLineSegment(sketch, "E21.right", {"start": v(-65, 10) * mm, "end": v(-65, -10) * mm});
            skSolve(sketch);
        }
        {
            var Q0;
            Q0=makeQuery(id+"F8.imprint","IMPRINT",FACE,{"disambiguationData":[TD([[makeQuery(id+"F8.imprint","IMPRINT",EDGE,{"derivedFrom":sQuery(id+"F8.wireOp",EDGE,"E21.bottom")}),1.0]])]});
            var Q1;
            Q1=makeQuery(id+"F8.imprint","IMPRINT",FACE,{"disambiguationData":[TD([[makeQuery(id+"F8.imprint","IMPRINT",EDGE,{"derivedFrom":sQuery(id+"F8.wireOp",EDGE,"E19.left")}),1.0]])]});
            extrude(context, id + "F9", {"entities" : qUnion([Q0, Q1]), "operationType" : NewBodyOperationType.ADD, "depth" : 60 * mm});
        }
        {
            var Q0;
            Q0=makeQuery(id+"F9.opExtrude","SWEPT_FACE",FACE,{"disambiguationData":[OSD([sQuery(id+"F8.wireOp",EDGE,"E21.left")])]});
            var sketch = newSketch(context, id + "F10", { "sketchPlane" : qUnion([Q0])});
            skLineSegment(sketch, "E22.bottom", {"start": v(-10, -60) * mm, "end": v(10, -60) * mm});
            skLineSegment(sketch, "E22.top", {"start": v(-10, -45) * mm, "end": v(10, -45) * mm});
            skLineSegment(sketch, "E22.left", {"start": v(-10, -60) * mm, "end": v(-10, -45) * mm});
            skLineSegment(sketch, "E22.right", {"start": v(10, -60) * mm, "end": v(10, -45) * mm});
            skSolve(sketch);
        }
        {
            var Q0;
            Q0=makeQuery(id+"F10.imprint","IMPRINT",FACE,{"disambiguationData":[TD([[makeQuery(id+"F10.imprint","IMPRINT",EDGE,{"derivedFrom":sQuery(id+"F10.wireOp",EDGE,"E22.bottom")}),1.0]])]});
            extrude(context, id + "F11", {"entities" : qUnion([Q0]), "operationType" : NewBodyOperationType.ADD, "endBound" : BoundingType.UP_TO_NEXT, "depth" : 25 * mm});
        }
        {
            var Q0;
            Q0=makeQuery(id+"F9.opExtrude","SWEPT_EDGE",EDGE,{"disambiguationData":[OSD([sQuery(id+"F8.wireOp",EDGE,"E19.left"),sQuery(id+"F8.wireOp",EDGE,"E20.top")])]});
            var Q1;
            Q1=makeQuery(id+"F9.opExtrude","SWEPT_EDGE",EDGE,{"disambiguationData":[OSD([sQuery(id+"F8.wireOp",EDGE,"E20.top"),sQuery(id+"F8.wireOp",EDGE,"E20.right")])]});
            var Q2;
            Q2=makeQuery(id+"F9.opExtrude","SWEPT_EDGE",EDGE,{"disambiguationData":[OSD([sQuery(id+"F8.wireOp",EDGE,"E20.bottom"),sQuery(id+"F8.wireOp",EDGE,"E20.right")])]});
            var Q3;
            Q3=makeQuery(id+"F9.opExtrude","SWEPT_EDGE",EDGE,{"disambiguationData":[OSD([sQuery(id+"F8.wireOp",EDGE,"E19.left"),sQuery(id+"F8.wireOp",EDGE,"E20.bottom")])]});
            var Q4;
            Q4=makeQuery(id+"F9.opExtrude","SWEPT_EDGE",EDGE,{"disambiguationData":[OSD([sQuery(id+"F8.wireOp",EDGE,"E21.bottom"),sQuery(id+"F8.wireOp",EDGE,"E21.left")])]});
            var Q5;
            Q5=makeQuery(id+"F9.opExtrude","SWEPT_EDGE",EDGE,{"disambiguationData":[OSD([sQuery(id+"F8.wireOp",EDGE,"E21.bottom"),sQuery(id+"F8.wireOp",EDGE,"E21.right")])]});
            var Q6;
            Q6=makeQuery(id+"F9.opExtrude","SWEPT_EDGE",EDGE,{"disambiguationData":[OSD([sQuery(id+"F8.wireOp",EDGE,"E21.top"),sQuery(id+"F8.wireOp",EDGE,"E21.right")])]});
            var Q7;
            Q7=makeQuery(id+"F9.opExtrude","SWEPT_EDGE",EDGE,{"disambiguationData":[OSD([sQuery(id+"F8.wireOp",EDGE,"E21.top"),sQuery(id+"F8.wireOp",EDGE,"E21.left")])]});
            fillet(context, id + "F12", {"entities" : qUnion([Q0, Q1, Q2, Q3, Q4, Q5, Q6, Q7]), "radius" : 7.5 * mm, "tangentPropagation" : true, "allowEdgeOverflow" : false});
        }
        {
            var Q0;
            Q0=makeQuery(id+"F11.boolean.opBoolean","MERGE",EDGE,{"derivedFrom":[makeQuery(id+"F9.opExtrude","CAP_EDGE",EDGE,{"disambiguationData":[OSD([sQuery(id+"F8.wireOp",EDGE,"E20.top")])],"isStart":false}),makeQuery(id+"F9.opExtrude","CAP_EDGE",EDGE,{"disambiguationData":[OSD([sQuery(id+"F8.wireOp",EDGE,"E21.top")])],"isStart":false}),makeQuery(id+"F11.opExtrude","SWEPT_EDGE",EDGE,{"disambiguationData":[OSD([sQuery(id+"F10.wireOp",EDGE,"E22.bottom"),sQuery(id+"F10.wireOp",EDGE,"E22.right")])]})]});
            var Q1;
            Q1=makeQuery(id+"F11.opExtrude","SWEPT_EDGE",EDGE,{"disambiguationData":[OSD([sQuery(id+"F8.wireOp",EDGE,"E21.top"),sQuery(id+"F8.wireOp",EDGE,"E21.left"),sQuery(id+"F10.wireOp",EDGE,"E22.top"),sQuery(id+"F10.wireOp",EDGE,"E22.right")])]});
            var Q2;
            Q2=makeQuery(id+"F11.opExtrude","SWEPT_EDGE",EDGE,{"disambiguationData":[OSD([sQuery(id+"F8.wireOp",EDGE,"E21.bottom"),sQuery(id+"F8.wireOp",EDGE,"E21.left"),sQuery(id+"F10.wireOp",EDGE,"E22.top"),sQuery(id+"F10.wireOp",EDGE,"E22.left")])]});
            fillet(context, id + "F13", {"entities" : qUnion([Q0, Q1, Q2]), "radius" : 7.5 * mm, "tangentPropagation" : true, "allowEdgeOverflow" : false});
        }
        {
            var Q0;
            Q0=makeQuery(id+"F4.opExtrude","SWEPT_FACE",FACE,{"disambiguationData":[OSD([sQuery(id+"F0.wireOp",EDGE,"E18")])]});
            cPlane(context, id + "F14", {"entities" : qUnion([Q0]), "cplaneType" : CPlaneType.OFFSET, "offset" : 2.5 * mm, "width" : 150 * mm, "height" : 150 * mm});
        }
        {
            var Q0;
            Q0=qCreatedBy(id+"F14.planeOp",FACE);
            var sketch = newSketch(context, id + "F15", { "sketchPlane" : qUnion([Q0])});
            skLineSegment(sketch, "E23", {"start": v(0, 0) * mm, "end": v(0, 31.87) * mm});
            skLineSegment(sketch, "E24", {"start": v(0, 0) * mm, "end": v(65, 0) * mm});
            skLineSegment(sketch, "E25", {"start": v(65, 0) * mm, "end": v(65, 20) * mm});
            skCircle(sketch, "E26", {"center": v(65, 20) * mm, "radius": 1.25 * mm});
            skSolve(sketch);
        }
        {
            var Q0;
            Q0=makeQuery(id+"F15.imprint","IMPRINT",FACE,{"disambiguationData":[TD([[makeQuery(id+"F15.imprint","IMPRINT",EDGE,{"derivedFrom":sQuery(id+"F15.wireOp",EDGE,"E26")}),1.0]])]});
            var Q1;
            Q1=sQuery(id+"F15.wireOp",EDGE,"E23");
            revolve(context, id + "F16", {"operationType" : NewBodyOperationType.REMOVE, "entities" : qUnion([Q0]), "axis" : qUnion([Q1]), "revolveType" : RevolveType.FULL, "oppositeDirection" : true});
        }
    });
